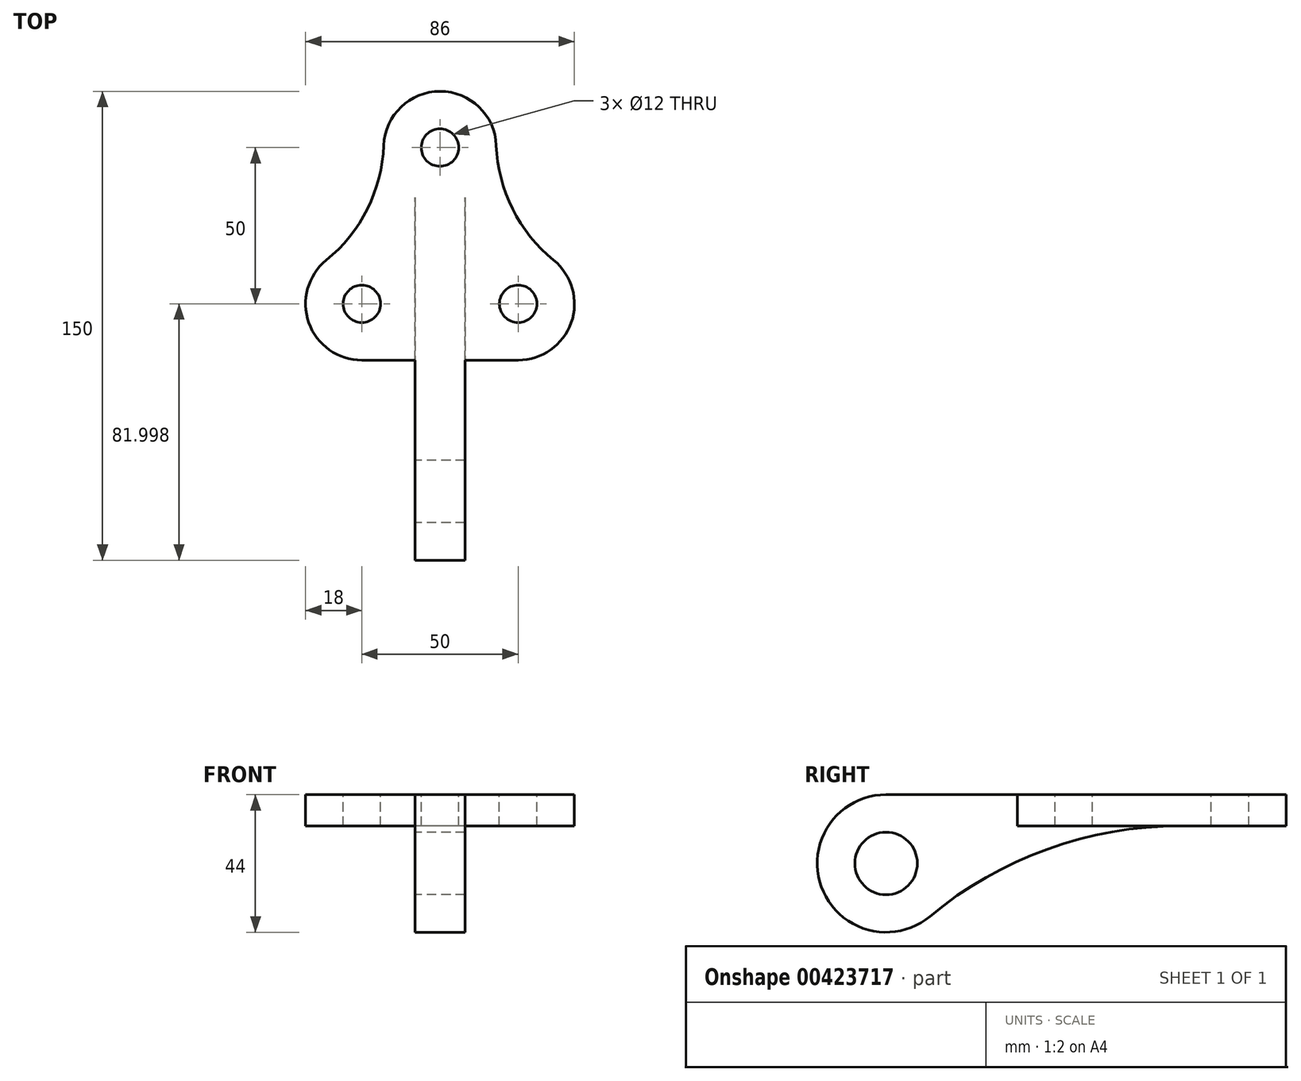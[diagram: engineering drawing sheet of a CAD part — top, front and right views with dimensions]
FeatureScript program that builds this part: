
annotation { "Feature Type Name" : "Feature", "Feature Type Description" : "" }
export const myFeature = defineFeature(function(context is Context, id is Id, definition is map)
    precondition{}
    {
        {
            var Q0;
            Q0=qCreatedBy(makeId("Top.planeOp"),FACE);
            var sketch = newSketch(context, id + "F0", { "sketchPlane" : qUnion([Q0])});
            skLineSegment(sketch, "E0", {"start": v(0, 91.5) * mm, "end": v(0, -90.28) * mm, "construction": true});
            skArc(sketch, "E1", {"start": v(17.99, 64.59) * mm, "mid": v(12.47, 76.85) * mm, "end": v(0, 81.87) * mm});
            skArc(sketch, "E2", {"start": v(25, -4.13) * mm, "mid": v(41.96, 7.84) * mm, "end": v(36.37, 27.82) * mm});
            skLineSegment(sketch, "E3", {"start": v(25, -4.13) * mm, "end": v(0, -4.13) * mm});
            skArc(sketch, "E4", {"start": v(0, 57.87) * mm, "mid": v(6, 63.87) * mm, "end": v(0, 69.87) * mm});
            skCircle(sketch, "E5", {"center": v(25, 13.87) * mm, "radius": 6 * mm});
            skPoint(sketch, "E6.first.point", {"position": v(-14.96, 53.86) * mm});
            skPoint(sketch, "E6.second.point", {"position": v(23.6, 31.81) * mm});
            skPoint(sketch, "E6.third.point", {"position": v(73.47, 64.24) * mm});
            skArc(sketch, "E7", {"start": v(17.99, 64.59) * mm, "mid": v(23.22, 44.23) * mm, "end": v(36.37, 27.82) * mm});
            skArc(sketch, "E8.MirrorCS", {"start": v(-17.99, 64.59) * mm, "mid": v(-12.47, 76.85) * mm, "end": v(0, 81.87) * mm});
            skArc(sketch, "E9.MirrorCS", {"start": v(-17.99, 64.59) * mm, "mid": v(-23.22, 44.23) * mm, "end": v(-36.37, 27.82) * mm});
            skArc(sketch, "E10.MirrorCS", {"start": v(-25, -4.13) * mm, "mid": v(-41.96, 7.84) * mm, "end": v(-36.37, 27.82) * mm});
            skLineSegment(sketch, "E11.MirrorCS", {"start": v(-25, -4.13) * mm, "end": v(0, -4.13) * mm});
            skCircle(sketch, "E12.MirrorC", {"center": v(-25, 13.87) * mm, "radius": 6 * mm});
            skArc(sketch, "E13.MirrorCS", {"start": v(0, 57.87) * mm, "mid": v(-6, 63.87) * mm, "end": v(0, 69.87) * mm});
            skSolve(sketch);
        }
        {
            var Q0;
            Q0=qCreatedBy(makeId("Right.planeOp"),FACE);
            var sketch = newSketch(context, id + "F1", { "sketchPlane" : qUnion([Q0])});
            skPoint(sketch, "E14.0", {"position": v(63.87, 0) * mm});
            skCircle(sketch, "E15", {"center": v(-46.13, -22) * mm, "radius": 10 * mm});
            skPoint(sketch, "E16.right.end.orphan", {"position": v(-46.13, -10) * mm});
            skLineSegment(sketch, "E17.bottom", {"start": v(-46.13, 0) * mm, "end": v(63.87, 0) * mm});
            skLineSegment(sketch, "E17.right", {"start": v(63.87, 0) * mm, "end": v(63.87, -10) * mm});
            skArc(sketch, "E18", {"start": v(-46.13, 0) * mm, "mid": v(-66.82, -29.48) * mm, "end": v(-32.06, -38.91) * mm});
            skArc(sketch, "E19", {"start": v(47.89, -10) * mm, "mid": v(5.38, -17.45) * mm, "end": v(-32.06, -38.91) * mm});
            skLineSegment(sketch, "E20.trimOffspring", {"start": v(47.89, -10) * mm, "end": v(63.87, -10) * mm});
            skSolve(sketch);
        }
        {
            var Q0;
            Q0=makeQuery(id+"F0.imprint","IMPRINT",FACE,{"disambiguationData":[TD([[makeQuery(id+"F0.imprint","IMPRINT",EDGE,{"derivedFrom":sQuery(id+"F0.wireOp",EDGE,"E1")}),1.0]])]});
            extrude(context, id + "F2", {"entities" : qUnion([Q0]), "oppositeDirection" : true, "depth" : 10 * mm});
        }
        {
            var Q0;
            Q0=makeQuery(id+"F1.imprint","IMPRINT",FACE,{"disambiguationData":[TD([[makeQuery(id+"F1.imprint","IMPRINT",EDGE,{"derivedFrom":sQuery(id+"F1.wireOp",EDGE,"E15")}),-1.0]])]});
            extrude(context, id + "F3", {"entities" : qUnion([Q0]), "operationType" : NewBodyOperationType.ADD, "endBound" : BoundingType.SYMMETRIC, "depth" : 16 * mm});
        }
        {
            var Q0;
            Q0=qCreatedBy(makeId("Top.planeOp"),FACE);
            var sketch = newSketch(context, id + "F4", { "sketchPlane" : qUnion([Q0])});
            skPoint(sketch, "E21.0", {"position": v(0, 63.87) * mm});
            skCircle(sketch, "E22", {"center": v(0, 63.87) * mm, "radius": 6 * mm});
            skSolve(sketch);
        }
        {
            var Q0;
            Q0 = qSketchRegion(id + "F4", true);
            extrude(context, id + "F5", {"entities" : qUnion([Q0]), "operationType" : NewBodyOperationType.REMOVE, "oppositeDirection" : true, "depth" : 25 * mm});
        }
    });
